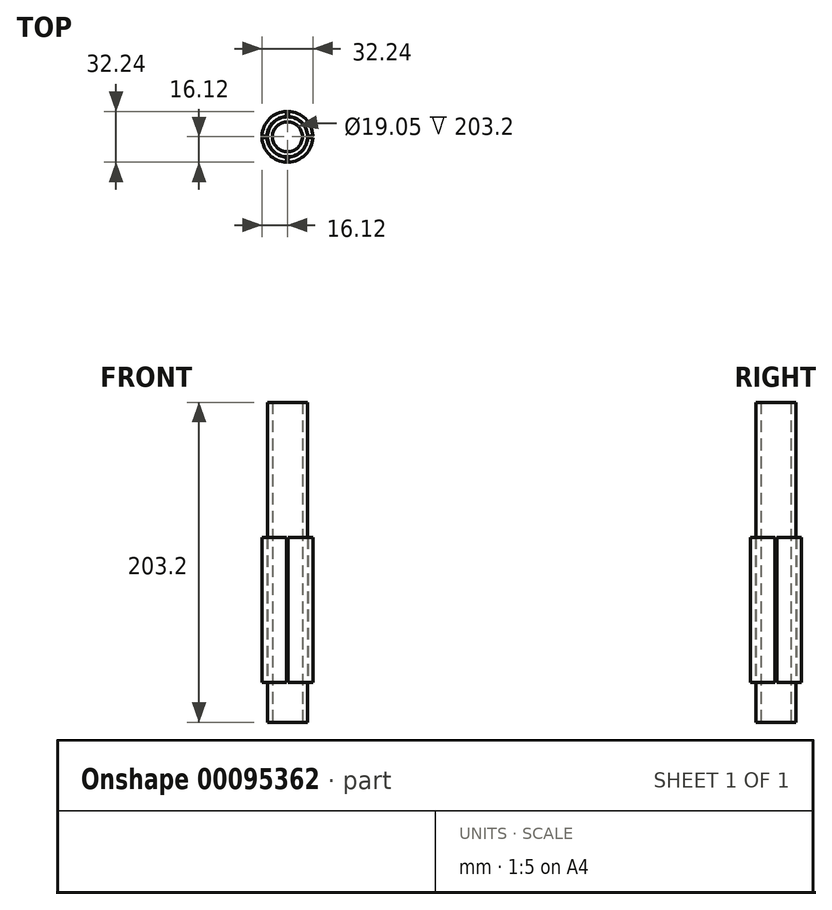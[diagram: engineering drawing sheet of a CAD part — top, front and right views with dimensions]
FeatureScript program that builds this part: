
annotation { "Feature Type Name" : "Feature", "Feature Type Description" : "" }
export const myFeature = defineFeature(function(context is Context, id is Id, definition is map)
    precondition{}
    {
        {
            var Q0;
            Q0=qCreatedBy(makeId("Top.planeOp"),FACE);
            var sketch = newSketch(context, id + "F0", { "sketchPlane" : qUnion([Q0])});
            skCircle(sketch, "E0", {"center": v(0, 0) * mm, "radius": 12.7 * mm});
            skCircle(sketch, "E1", {"center": v(0, 0) * mm, "radius": 9.53 * mm});
            skSolve(sketch);
        }
        {
            var Q0;
            Q0=makeQuery(id+"F0.imprint","IMPRINT",FACE,{"disambiguationData":[TD([[makeQuery(id+"F0.imprint","IMPRINT",EDGE,{"derivedFrom":sQuery(id+"F0.wireOp",EDGE,"E0")}),1.0]])]});
            extrude(context, id + "F1", {"entities" : qUnion([Q0]), "depth" : 177.8 * mm});
        }
        {
            var Q0;
            Q0=qCreatedBy(makeId("Top.planeOp"),FACE);
            var sketch = newSketch(context, id + "F2", { "sketchPlane" : qUnion([Q0])});
            skCircle(sketch, "E2", {"center": v(0, 0) * mm, "radius": 12.95 * mm});
            skCircle(sketch, "E3", {"center": v(0, 0) * mm, "radius": 16.13 * mm});
            skSolve(sketch);
        }
        {
            var Q0;
            Q0 = qSketchRegion(id + "F2", true);
            extrude(context, id + "F3", {"entities" : qUnion([Q0]), "depth" : 92.07 * mm});
        }
        {
            var Q0;
            Q0=qCreatedBy(makeId("Top.planeOp"),FACE);
            var sketch = newSketch(context, id + "F4", { "sketchPlane" : qUnion([Q0])});
            skLineSegment(sketch, "E4.bottom", {"start": v(16.7, -0.51) * mm, "end": v(12.92, -0.51) * mm});
            skLineSegment(sketch, "E4.top", {"start": v(16.7, 0.59) * mm, "end": v(12.92, 0.59) * mm});
            skLineSegment(sketch, "E4.left", {"start": v(16.7, -0.51) * mm, "end": v(16.7, 0.59) * mm});
            skLineSegment(sketch, "E4.right", {"start": v(12.92, -0.51) * mm, "end": v(12.92, 0.59) * mm});
            skSolve(sketch);
        }
        {
            var Q0;
            Q0=makeQuery(id+"F4.imprint","IMPRINT",FACE,{"disambiguationData":[TD([[makeQuery(id+"F4.imprint","IMPRINT",EDGE,{"derivedFrom":sQuery(id+"F4.wireOp",EDGE,"E4.bottom")}),-1.0]])]});
            var Q1;
            Q1 = qSketchRegion(id + "F6", true);
            extrude(context, id + "F5", {"entities" : qUnion([Q0, Q1]), "operationType" : NewBodyOperationType.REMOVE, "endBound" : BoundingType.THROUGH_ALL, "depth" : 25.4 * mm});
        }
        {
            var Q0;
            Q0=qCreatedBy(makeId("Top.planeOp"),FACE);
            var sketch = newSketch(context, id + "F6", { "sketchPlane" : qUnion([Q0])});
            skLineSegment(sketch, "E5.bottom", {"start": v(-16.47, -0.4) * mm, "end": v(-12.86, -0.4) * mm});
            skLineSegment(sketch, "E5.top", {"start": v(-16.47, 0.47) * mm, "end": v(-12.86, 0.47) * mm});
            skLineSegment(sketch, "E5.left", {"start": v(-16.47, -0.4) * mm, "end": v(-16.47, 0.47) * mm});
            skLineSegment(sketch, "E5.right", {"start": v(-12.86, -0.4) * mm, "end": v(-12.86, 0.47) * mm});
            skLineSegment(sketch, "E6", {"start": v(-0.43, -12.85) * mm, "end": v(-0.43, -16.47) * mm});
            skLineSegment(sketch, "E7", {"start": v(-0.43, -16.47) * mm, "end": v(0.49, -16.47) * mm});
            skLineSegment(sketch, "E8", {"start": v(0.49, -16.47) * mm, "end": v(0.49, -12.81) * mm});
            skLineSegment(sketch, "E9", {"start": v(0.49, -12.81) * mm, "end": v(-0.43, -12.85) * mm});
            skLineSegment(sketch, "E10", {"start": v(-0.45, 12.81) * mm, "end": v(0.53, 12.81) * mm});
            skLineSegment(sketch, "E11", {"start": v(0.53, 12.81) * mm, "end": v(0.53, 16.6) * mm});
            skLineSegment(sketch, "E12", {"start": v(0.53, 16.6) * mm, "end": v(-0.45, 16.6) * mm});
            skLineSegment(sketch, "E13", {"start": v(-0.45, 16.6) * mm, "end": v(-0.45, 12.81) * mm});
            skSolve(sketch);
        }
        {
            var Q0;
            Q0=makeQuery(id+"F6.imprint","IMPRINT",FACE,{"disambiguationData":[TD([[makeQuery(id+"F6.imprint","IMPRINT",EDGE,{"derivedFrom":sQuery(id+"F6.wireOp",EDGE,"E5.bottom")}),1.0]])]});
            var Q1;
            Q1=makeQuery(id+"F6.imprint","IMPRINT",FACE,{"disambiguationData":[TD([[makeQuery(id+"F6.imprint","IMPRINT",EDGE,{"derivedFrom":sQuery(id+"F6.wireOp",EDGE,"E6")}),1.0]])]});
            var Q2;
            Q2=makeQuery(id+"F6.imprint","IMPRINT",FACE,{"disambiguationData":[TD([[makeQuery(id+"F6.imprint","IMPRINT",EDGE,{"derivedFrom":sQuery(id+"F6.wireOp",EDGE,"E10")}),1.0]])]});
            extrude(context, id + "F7", {"entities" : qUnion([Q0, Q1, Q2]), "operationType" : NewBodyOperationType.REMOVE, "endBound" : BoundingType.UP_TO_NEXT, "depth" : 101.6 * mm});
        }
        {
            var Q0;
            Q0=makeQuery(id+"F1.opExtrude","CAP_FACE",FACE,{"disambiguationData":[OSD([sQuery(id+"F0.wireOp",EDGE,"E0"),sQuery(id+"F0.wireOp",EDGE,"E1")])],"isStart":true});
            extrude(context, id + "F8", {"entities" : qUnion([Q0]), "operationType" : NewBodyOperationType.ADD, "depth" : 25.4 * mm});
        }
    });
